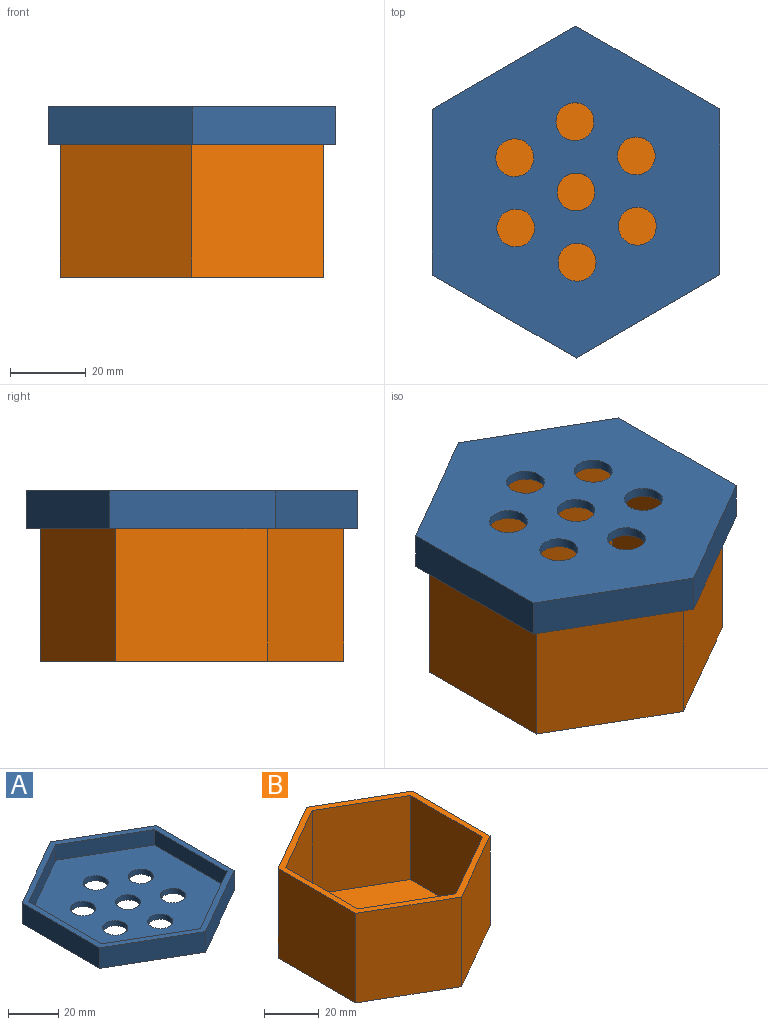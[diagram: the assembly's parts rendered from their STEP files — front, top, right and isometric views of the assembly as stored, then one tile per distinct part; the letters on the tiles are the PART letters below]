
ASSEMBLY  parts=2 mates=1
PART A: 22 faces, bbox 75.8x87.5x10 mm
  f0: cylinder r=5mm len=10mm, axis (0,0,1), area 78.5mm2, adj f12,f19
  f1: cylinder r=5mm len=10mm, axis (0,0,1), area 78.5mm2, adj f12,f19
  f2: cylinder r=5mm len=10mm, axis (0,0,1), area 78.5mm2, adj f12,f19
  f3: cylinder r=5mm len=10mm, axis (0,0,1), area 78.5mm2, adj f12,f19
  f4: cylinder r=5mm len=10mm, axis (0,0,1), area 78.5mm2, adj f12,f19
  f5: plane 37.92x21.83mm, normal (0.5,-0.87,0), area 437.5mm2, adj f6,f10,f11,f12
  f6: plane 43.75x10mm, normal (1,0,0), area 437.5mm2, adj f5,f7,f11,f12
  f7: plane 37.86x21.93mm, normal (0.5,0.87,0), area 437.5mm2, adj f6,f8,f11,f12
  f8: plane 37.92x21.83mm, normal (-0.5,0.87,0), area 437.5mm2, adj f7,f9,f11,f12
  f9: plane 43.75x10mm, normal (-1,0,0), area 437.5mm2, adj f8,f10,f11,f12
  f10: plane 37.86x21.93mm, normal (-0.5,-0.87,0), area 437.5mm2, adj f5,f9,f11,f12
  f11: plane 87.5x75.83mm, normal (0,0,1), area 634.6mm2, adj f5,f6,f7,f8,f9,f10,f13,f14
  f12: plane 87.5x75.83mm, normal (0,0,-1), area 4423.1mm2, adj f0,f1,f2,f3,f4,f5,f6,f7
  f13: plane 35.42x20.39mm, normal (-0.5,0.87,0), area 306.5mm2, adj f11,f14,f18,f19
  f14: plane 40.86x7.5mm, normal (-1,0,0), area 306.5mm2, adj f11,f13,f15,f19
  f15: plane 35.36x20.48mm, normal (-0.5,-0.87,0), area 306.5mm2, adj f11,f14,f16,f19
  f16: plane 35.42x20.39mm, normal (0.5,-0.87,0), area 306.5mm2, adj f11,f15,f17,f19
  f17: plane 40.86x7.5mm, normal (1,0,0), area 306.5mm2, adj f11,f16,f18,f19
  f18: plane 35.36x20.48mm, normal (0.5,0.87,0), area 306.5mm2, adj f11,f13,f17,f19
  f19: plane 81.73x70.83mm, normal (0,0,1), area 3788.5mm2, adj f0,f1,f2,f3,f4,f13,f14,f15
  f20: cylinder r=5mm len=10mm, axis (0,0,1), area 78.5mm2, adj f12,f19
  f21: cylinder r=5mm len=10mm, axis (0,0,-1), area 78.5mm2, adj f12,f19
PART B: 15 faces, bbox 69.3x80x40 mm
  f0: plane 40x34.67mm, normal (0.5,-0.87,0), area 1600mm2, adj f1,f5,f6,f7
  f1: plane 40x40mm, normal (1,0,0), area 1600mm2, adj f0,f2,f6,f7
  f2: plane 40x34.61mm, normal (0.5,0.87,0), area 1600mm2, adj f1,f3,f6,f7
  f3: plane 40x34.67mm, normal (-0.5,0.87,0), area 1600mm2, adj f2,f4,f6,f7
  f4: plane 40x40mm, normal (-1,0,0), area 1600mm2, adj f3,f5,f6,f7
  f5: plane 40x34.61mm, normal (-0.5,-0.87,0), area 1600mm2, adj f0,f4,f6,f7
  f6: plane 80x69.33mm, normal (0,0,1), area 578.3mm2, adj f0,f1,f2,f3,f4,f5,f8,f9
  f7: plane 80x69.33mm, normal (0,0,-1), area 4156.9mm2, adj f0,f1,f2,f3,f4,f5
  f8: plane 37.5x32.17mm, normal (-0.5,0.87,0), area 1391.7mm2, adj f6,f9,f13,f14
  f9: plane 37.5x37.11mm, normal (-1,0,0), area 1391.7mm2, adj f6,f8,f10,f14
  f10: plane 37.5x32.12mm, normal (-0.5,-0.87,0), area 1391.7mm2, adj f6,f9,f11,f14
  f11: plane 37.5x32.17mm, normal (0.5,-0.87,0), area 1391.7mm2, adj f6,f10,f12,f14
  f12: plane 37.5x37.11mm, normal (1,0,0), area 1391.7mm2, adj f6,f11,f13,f14
  f13: plane 37.5x32.12mm, normal (0.5,0.87,0), area 1391.7mm2, adj f6,f8,f12,f14
  f14: plane 74.23x64.33mm, normal (0,0,1), area 3578.6mm2, adj f8,f9,f10,f11,f12,f13
PLACE A rot(axis=(0,1,0),180deg) t=(-3.13,6.06,36.67)mm
PLACE B t=(-3.13,6.06,-8.2)mm fixed
MATE slider B.f6 <-> A.f21  axis (0,0,1) through (-3.13,6.06,31.8)mm
